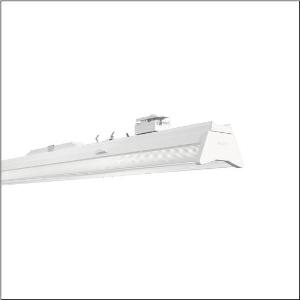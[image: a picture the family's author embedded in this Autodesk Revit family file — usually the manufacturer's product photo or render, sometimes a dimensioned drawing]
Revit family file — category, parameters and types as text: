
# Revit family: licross_21_performance_mo_52td16cn46xg
name_source: partatom
category: Lighting Fixtures
units: mm (PartAtom-declared; Revit-internal decimal feet)

## family parameters
Cut with Voids When Loaded = No
Host = Face
Light Source = No
Part Type = Normal
Room Calculation Point = No
Round Connector Dimension = Use Diameter
Shared = No

## types (1)
- --- (1 x LED, 6000 lm, 32 W, 4000K)
    Apparent Load = 32 VA
    CIE Flux Codes = 66 88 96 79 100
    Color Rendering = 80
    Color Temperature = 4000K
    Default Elevation = 1800 mm
    Description = Licross 21 Performance MO, luminaire insert, of sheet steel, galvanised, coil coated, white, length: 1.500mm, width: 120mm, height: 123mm, LED rated luminous flux: 6.000lm, light colour: 840, SDCM (Standard Deviation of Colour Matching)MacAdam ≤ 3 SDCM (initial), control gear: ON/OFF Multilumen, CLOi, with plug, 3-pole, with phase selection, mains connection: 220..240V, AC, 50/60Hz, start of lifetime: 32W, end of service life: 38W, internal wiring halogen-free, primary light control with lens, of plastic, primary optical cover: cover, of PMMA, light emission: direct/indirect distribution, primary light characteristic: symmetric, protection rating (complete): IP54, insulation class (complete): insulation class I (protective earthing), certification: CE, ENEC, UKCA, protection symbol: D if used in an environment with non-conductive dust loads with corresponding accessories, impact resistance: IK06, permissible ambient temperature for indoor applications: -35..+55°C, corresponds to IFS (International Featured Standards) requirements for safety and quality in the food industry, reducing of maximum allowable ambient temperature of 5°C with ceiling mounting, LABS conformity tested according to VDMA 24364:2018-05, The light source and the operating device comply with the requirements of the Ecodesign Regulation (EU) 2019/2020 and are replaceable in accordance with this regulation, packaging unit: 1 piece
    Height = 114 mm
    Lamp = 1 x LED
    Lamp Light Flux = 6000 lm
    Lamp Power = 32 W
    Lamp count = 1
    Length = 1500 mm
    Luminous efficacy = 188 lm/W
    Manufacturer = Siteco
    ModVariant = No
    Model = 52TD16CN46XG
    Mounting Place = Ceiling
    Mounting Type = Pendant
    Number of Poles = 1
    OnlyDefault = Yes
    Power Factor = 1
    Product Name = Licross 21 Performance MO
    Product group = luminaire insert | ceiling pendant
    ProductGroupID = 901
    Protection Class = Protection class I
    Protection Degree = IP 54
    RLX_Detail_Level = 1
    RLX_Emergency_Light_Flux = 0 lm
    RLX_Emergency_Type = 0
    RLX_Emergency_Type_DB = No
    RlxData = <blob elided: 32053 chars, md5=fe449b6a>
    Socket = socket
    Standby Power = 0 W
    System Light Flux = 6000 lm
    System Power = 32 W
    Type Comments = factory setting: luminous flux: 100 % | (A | C | E) | 74 mA
    Type Image = l_1256138.jpg
    URL = http://relux.com
    VarID = @adj_113053
    Voltage = 0 V
    Weight = 0.00 kg
    Width = 120 mm

## geometry (parser evidence)
native form markers: Blend x4, Sweep x11
no freeform markers — native parametric forms only
